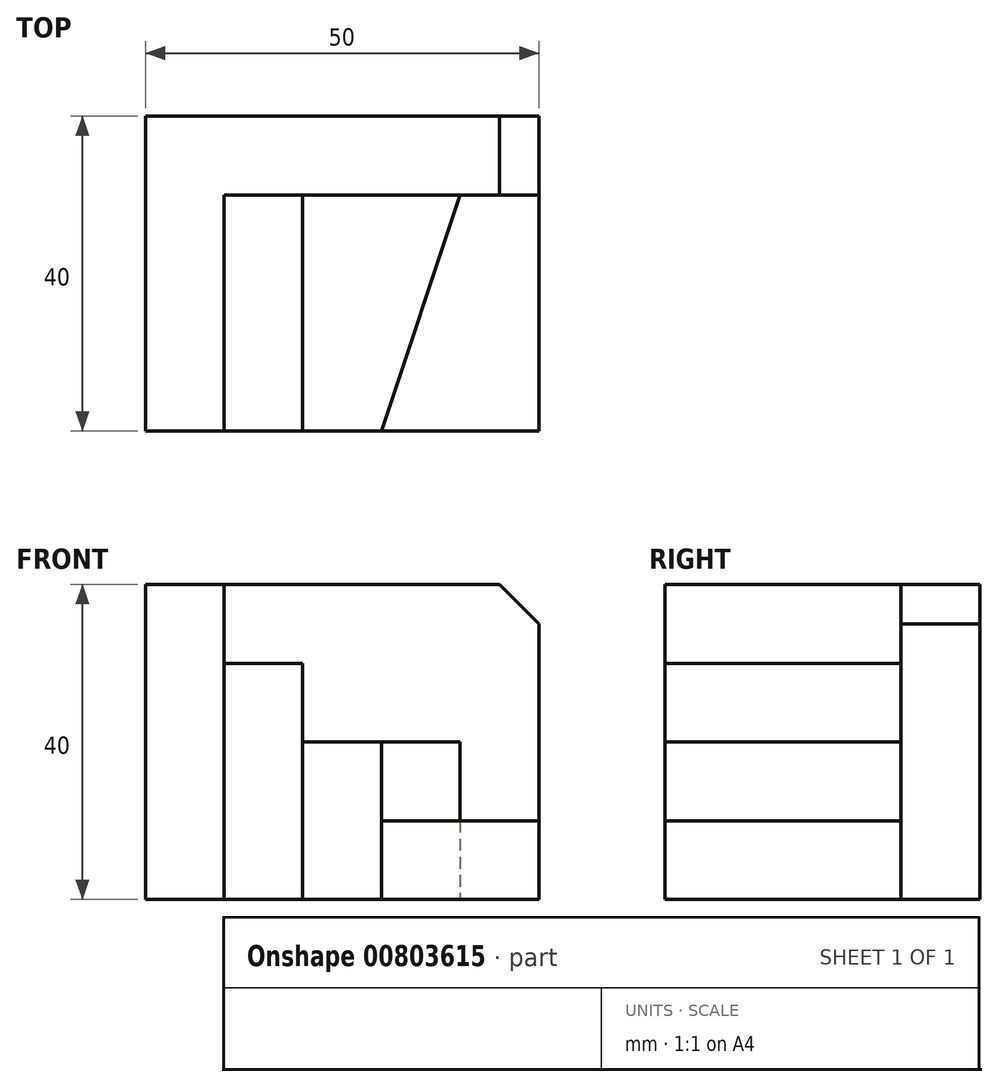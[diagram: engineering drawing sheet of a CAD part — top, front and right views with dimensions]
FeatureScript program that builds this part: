
annotation { "Feature Type Name" : "Feature", "Feature Type Description" : "" }
export const myFeature = defineFeature(function(context is Context, id is Id, definition is map)
    precondition{}
    {
        {
            var Q0;
            Q0=qCreatedBy(makeId("Top.planeOp"),FACE);
            var sketch = newSketch(context, id + "F0", { "sketchPlane" : qUnion([Q0])});
            skLineSegment(sketch, "E0.bottom", {"start": v(0, 0) * mm, "end": v(50, 0) * mm});
            skLineSegment(sketch, "E0.top", {"start": v(0, 40) * mm, "end": v(50, 40) * mm});
            skLineSegment(sketch, "E0.left", {"start": v(0, 0) * mm, "end": v(0, 40) * mm});
            skLineSegment(sketch, "E0.right", {"start": v(50, 0) * mm, "end": v(50, 40) * mm});
            skLineSegment(sketch, "E1", {"start": v(10, 0) * mm, "end": v(10, 30) * mm});
            skLineSegment(sketch, "E2", {"start": v(10, 30) * mm, "end": v(50, 30) * mm});
            skLineSegment(sketch, "E3", {"start": v(20, 30) * mm, "end": v(20, 0) * mm});
            skLineSegment(sketch, "E4", {"start": v(30, 0) * mm, "end": v(40, 30) * mm});
            skSolve(sketch);
        }
        {
            var Q0;
            {var subQ1=sQuery(id+"F0.wireOp",EDGE,"E0.top");Q0=makeQuery(id+"F0.imprint","IMPRINT",FACE,{"disambiguationData":[TD([[makeQuery(id+"F0.imprint","IMPRINT",EDGE,{"derivedFrom":subQ1}),-1.0]])]});}
            extrude(context, id + "F1", {"entities" : qUnion([Q0]), "depth" : 40 * mm, "offsetDistance" : 25 * mm});
        }
        {
            var Q0;
            {var subQ0=sQuery(id+"F0.wireOp",EDGE,"E1");Q0=makeQuery(id+"F0.imprint","IMPRINT",FACE,{"disambiguationData":[TD([[makeQuery(id+"F0.imprint","IMPRINT",EDGE,{"derivedFrom":subQ0}),-1.0]])]});}
            extrude(context, id + "F2", {"entities" : qUnion([Q0]), "depth" : 30 * mm, "offsetDistance" : 25 * mm});
        }
        {
            var Q0;
            {var subQ0=sQuery(id+"F0.wireOp",EDGE,"E3");Q0=makeQuery(id+"F0.imprint","IMPRINT",FACE,{"disambiguationData":[TD([[makeQuery(id+"F0.imprint","IMPRINT",EDGE,{"derivedFrom":subQ0}),1.0]])]});}
            extrude(context, id + "F3", {"entities" : qUnion([Q0]), "depth" : 20 * mm, "offsetDistance" : 25 * mm});
        }
        {
            var Q0;
            {var subQ3=sQuery(id+"F0.wireOp",EDGE,"E4");Q0=makeQuery(id+"F0.imprint","IMPRINT",FACE,{"disambiguationData":[TD([[makeQuery(id+"F0.imprint","IMPRINT",EDGE,{"derivedFrom":subQ3}),-1.0]])]});}
            extrude(context, id + "F4", {"entities" : qUnion([Q0]), "depth" : 10 * mm, "offsetDistance" : 25 * mm});
        }
        {
            var Q0;
            Q0=makeQuery(id+"F1.opExtrude","CAP_EDGE",EDGE,{"disambiguationData":[OSD([sQuery(id+"F0.wireOp",EDGE,"E0.right")])],"isStart":false});
            chamfer(context, id + "F5", {"entities" : qUnion([Q0]), "width" : 5 * mm, "tangentPropagation" : true});
        }
    });
